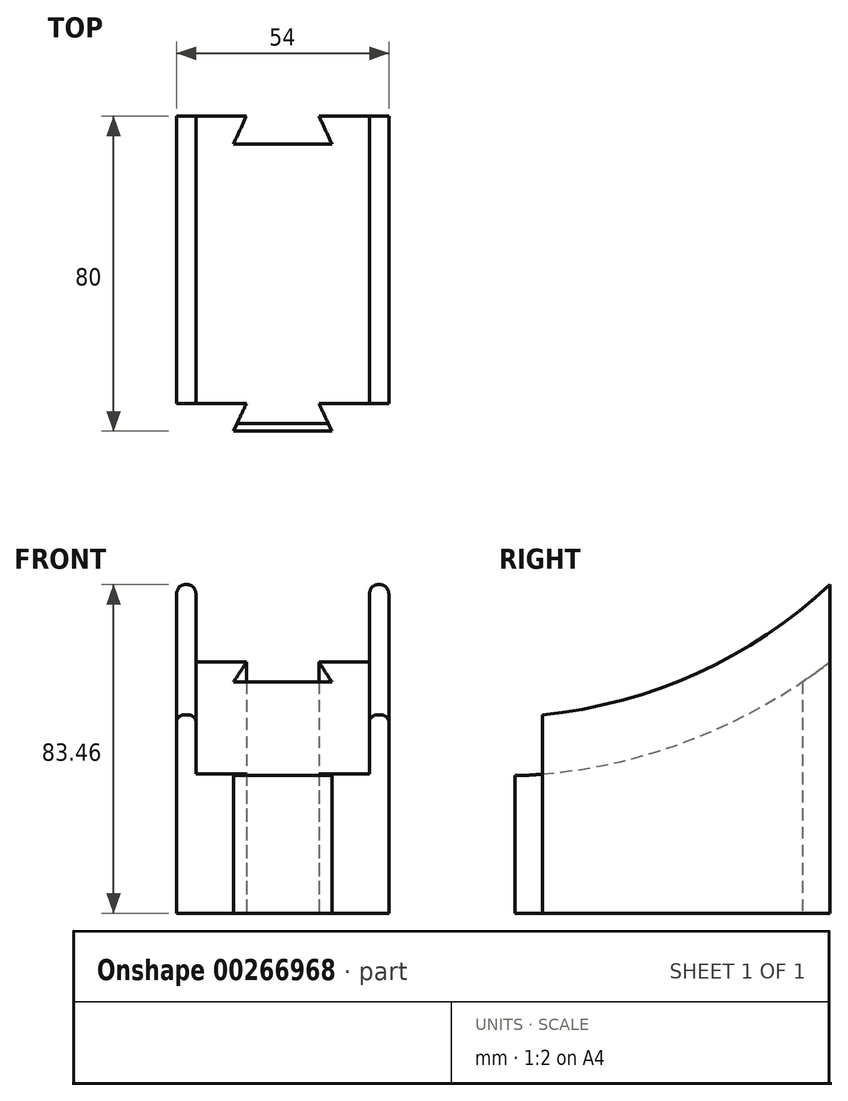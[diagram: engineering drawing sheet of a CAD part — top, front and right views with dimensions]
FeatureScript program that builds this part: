
annotation { "Feature Type Name" : "Feature", "Feature Type Description" : "" }
export const myFeature = defineFeature(function(context is Context, id is Id, definition is map)
    precondition{}
    {
        {
            var Q0;
            Q0=qCreatedBy(makeId("Right.planeOp"),FACE);
            var sketch = newSketch(context, id + "F0", { "sketchPlane" : qUnion([Q0])});
            skLineSegment(sketch, "E0.top", {"start": v(0, 120) * mm, "end": v(-45, 120) * mm});
            skLineSegment(sketch, "E0.left", {"start": v(0, 0) * mm, "end": v(0, 120) * mm});
            skLineSegment(sketch, "E1.top", {"start": v(0, 0) * mm, "end": v(-150, 0) * mm});
            skArc(sketch, "E2", {"start": v(-150, 50) * mm, "mid": v(-88.02, 70.78) * mm, "end": v(-45, 120) * mm});
            skLineSegment(sketch, "E3", {"start": v(-150, 50) * mm, "end": v(-150, 0) * mm});
            skSolve(sketch);
        }
        {
            var Q0;
            Q0=makeQuery(id+"F0.imprint","IMPRINT",FACE,{"disambiguationData":[TD([[makeQuery(id+"F0.imprint","IMPRINT",EDGE,{"derivedFrom":sQuery(id+"F0.wireOp",EDGE,"E0.bottom")}),-1.0]])]});
            var Q1;
            Q1=makeQuery(id+"F0.imprint","IMPRINT",FACE,{"disambiguationData":[TD([[makeQuery(id+"F0.imprint","IMPRINT",EDGE,{"derivedFrom":sQuery(id+"F0.wireOp",EDGE,"E0.top")}),1.0]])]});
            extrude(context, id + "F1", {"entities" : qUnion([Q0, Q1]), "depth" : 27 * mm});
        }
        {
            var Q0;
            Q0=makeQuery(id+"F1.opExtrude","SWEPT_BODY",BODY,{"disambiguationData":[OSD([sQuery(id+"F0.wireOp",EDGE,"E0.bottom"),sQuery(id+"F0.wireOp",EDGE,"E0.top"),sQuery(id+"F0.wireOp",EDGE,"E0.left"),sQuery(id+"F0.wireOp",EDGE,"E1.bottom"),sQuery(id+"F0.wireOp",EDGE,"E1.top"),sQuery(id+"F0.wireOp",EDGE,"E1.right"),sQuery(id+"F0.wireOp",EDGE,"E2")])]});
            var Q1;
            Q1=qCreatedBy(makeId("Right.planeOp"),FACE);
            mirror(context, id + "F2", {"operationType" : NewBodyOperationType.ADD, "entities" : qUnion([Q0]), "mirrorPlane" : qUnion([Q1])});
        }
        {
            var Q0;
            Q0=qCreatedBy(makeId("Right.planeOp"),FACE);
            var sketch = newSketch(context, id + "F3", { "sketchPlane" : qUnion([Q0])});
            skArc(sketch, "E4.0", {"start": v(-150, 34.98) * mm, "mid": v(-83.11, 56.1) * mm, "end": v(-34.86, 107) * mm});
            skLineSegment(sketch, "E5.0", {"start": v(-4.86, 107) * mm, "end": v(-34.86, 107) * mm});
            skLineSegment(sketch, "E6", {"start": v(-4.86, 107) * mm, "end": v(-4.86, 120) * mm});
            skLineSegment(sketch, "E7", {"start": v(-150, 34.98) * mm, "end": v(-150, 58.04) * mm});
            skArc(sketch, "E8.0", {"start": v(-150, 58.04) * mm, "mid": v(-93.92, 76.5) * mm, "end": v(-54, 120) * mm});
            skLineSegment(sketch, "E9", {"start": v(-54, 120) * mm, "end": v(-4.86, 120) * mm});
            skSolve(sketch);
        }
        {
            var Q0;
            Q0=qSketchRegion(id+"F3",true);
            extrude(context, id + "F4", {"entities" : qUnion([Q0]), "operationType" : NewBodyOperationType.REMOVE, "oppositeDirection" : true, "depth" : 22 * mm});
        }
        {
            var Q0;
            Q0=qSketchRegion(id+"F3",true);
            extrude(context, id + "F5", {"entities" : qUnion([Q0]), "operationType" : NewBodyOperationType.REMOVE, "depth" : 22 * mm});
        }
        {
            var Q0;
            Q0=qCreatedBy(makeId("Right.planeOp"),FACE);
            var sketch = newSketch(context, id + "F6", { "sketchPlane" : qUnion([Q0])});
            skLineSegment(sketch, "E10.bottom", {"start": v(-150, 0) * mm, "end": v(-240, 0) * mm});
            skLineSegment(sketch, "E10.top", {"start": v(-150, 50) * mm, "end": v(-240, 50) * mm});
            skLineSegment(sketch, "E10.left", {"start": v(-150, 0) * mm, "end": v(-150, 50) * mm});
            skLineSegment(sketch, "E10.right", {"start": v(-240, 0) * mm, "end": v(-240, 50) * mm});
            skSolve(sketch);
        }
        {
            var Q0;
            Q0=makeQuery(id+"F6.imprint","IMPRINT",FACE,{"disambiguationData":[TD([[makeQuery(id+"F6.imprint","IMPRINT",EDGE,{"derivedFrom":sQuery(id+"F6.wireOp",EDGE,"E10.bottom")}),-1.0]])]});
            extrude(context, id + "F7", {"entities" : qUnion([Q0]), "operationType" : NewBodyOperationType.ADD, "endBound" : BoundingType.SYMMETRIC, "oppositeDirection" : true, "depth" : 150 * mm});
        }
        {
            var Q0;
            Q0=makeQuery(id+"F7.opExtrude","SWEPT_FACE",FACE,{"disambiguationData":[OSD([sQuery(id+"F6.wireOp",EDGE,"E10.top")])]});
            var sketch = newSketch(context, id + "F8", { "sketchPlane" : qUnion([Q0])});
            skLineSegment(sketch, "E11.bottom", {"start": v(-70, -155) * mm, "end": v(70, -155) * mm});
            skLineSegment(sketch, "E11.top", {"start": v(-70, -235) * mm, "end": v(70, -235) * mm});
            skLineSegment(sketch, "E11.left", {"start": v(-70, -155) * mm, "end": v(-70, -235) * mm});
            skLineSegment(sketch, "E11.right", {"start": v(70, -155) * mm, "end": v(70, -235) * mm});
            skPoint(sketch, "E11.middle", {"position": v(0, -195) * mm});
            skSolve(sketch);
        }
        {
            var Q0;
            Q0=makeQuery(id+"F8.imprint","IMPRINT",FACE,{"disambiguationData":[TD([[makeQuery(id+"F8.imprint","IMPRINT",EDGE,{"derivedFrom":sQuery(id+"F8.wireOp",EDGE,"E11.bottom")}),-1.0]])]});
            extrude(context, id + "F9", {"entities" : qUnion([Q0]), "operationType" : NewBodyOperationType.REMOVE, "oppositeDirection" : true, "depth" : 45 * mm});
        }
        {
            var Q0;
            {var subQ5=sQuery(id+"F3.wireOp",EDGE,"E4.0");Q0=makeQuery(id+"F7.boolean.opBoolean","SPLIT",FACE,{"disambiguationData":[TD([makeQuery(id+"F4.boolean.opBoolean","COPY",FACE,{"derivedFrom":makeQuery(id+"F4.opExtrude","SWEPT_FACE",FACE,{"disambiguationData":[OSD([subQ5])]})})])],"derivedFrom":makeQuery(id+"F7.opExtrude","SWEPT_FACE",FACE,{"disambiguationData":[OSD([sQuery(id+"F6.wireOp",EDGE,"E10.left")])]})});}
            extrude(context, id + "F10", {"entities" : qUnion([Q0]), "operationType" : NewBodyOperationType.REMOVE, "oppositeDirection" : true, "depth" : 25 * mm});
        }
        {
            var Q0;
            Q0=makeQuery(id+"F7.opExtrude","CAP_EDGE",EDGE,{"disambiguationData":[OSD([sQuery(id+"F6.wireOp",EDGE,"E10.right")])],"isStart":true});
            var Q1;
            Q1=makeQuery(id+"F7.opExtrude","CAP_EDGE",EDGE,{"disambiguationData":[OSD([sQuery(id+"F6.wireOp",EDGE,"E10.left")])],"isStart":true});
            var Q2;
            Q2=makeQuery(id+"F7.opExtrude","CAP_EDGE",EDGE,{"disambiguationData":[OSD([sQuery(id+"F6.wireOp",EDGE,"E10.right")])],"isStart":false});
            var Q3;
            Q3=makeQuery(id+"F7.opExtrude","CAP_EDGE",EDGE,{"disambiguationData":[OSD([sQuery(id+"F6.wireOp",EDGE,"E10.left")])],"isStart":false});
            var Q4;
            Q4=makeQuery(id+"F1.opExtrude","CAP_EDGE",EDGE,{"disambiguationData":[OSD([sQuery(id+"F0.wireOp",EDGE,"E2")])],"isStart":false});
            var Q5;
            {var subQ2=sQuery(id+"F6.wireOp",EDGE,"E10.left");var subQ3=sQuery(id+"F6.wireOp",EDGE,"E10.top");Q5=makeQuery(id+"F7.boolean.opBoolean","SPLIT",EDGE,{"disambiguationData":[TD([makeQuery(id+"F7.opExtrude","CAP_FACE",FACE,{"disambiguationData":[OSD([sQuery(id+"F6.wireOp",EDGE,"E10.bottom"),subQ3,subQ2,sQuery(id+"F6.wireOp",EDGE,"E10.right")])],"isStart":true})])],"derivedFrom":makeQuery(id+"F7.opExtrude","SWEPT_EDGE",EDGE,{"disambiguationData":[OSD([subQ3,subQ2])]})});}
            var Q6;
            Q6=makeQuery(id+"F7.opExtrude","CAP_EDGE",EDGE,{"disambiguationData":[OSD([sQuery(id+"F6.wireOp",EDGE,"E10.top")])],"isStart":true});
            var Q7;
            Q7=makeQuery(id+"F7.opExtrude","SWEPT_EDGE",EDGE,{"disambiguationData":[OSD([sQuery(id+"F6.wireOp",EDGE,"E10.top"),sQuery(id+"F6.wireOp",EDGE,"E10.right")])]});
            var Q8;
            Q8=makeQuery(id+"F7.opExtrude","CAP_EDGE",EDGE,{"disambiguationData":[OSD([sQuery(id+"F6.wireOp",EDGE,"E10.top")])],"isStart":false});
            var Q9;
            {var subQ2=sQuery(id+"F6.wireOp",EDGE,"E10.left");var subQ3=sQuery(id+"F6.wireOp",EDGE,"E10.top");Q9=makeQuery(id+"F7.boolean.opBoolean","SPLIT",EDGE,{"disambiguationData":[TD([makeQuery(id+"F7.opExtrude","CAP_FACE",FACE,{"disambiguationData":[OSD([sQuery(id+"F6.wireOp",EDGE,"E10.bottom"),subQ3,subQ2,sQuery(id+"F6.wireOp",EDGE,"E10.right")])],"isStart":false})])],"derivedFrom":makeQuery(id+"F7.opExtrude","SWEPT_EDGE",EDGE,{"disambiguationData":[OSD([subQ3,subQ2])]})});}
            var Q10;
            Q10=makeQuery(id+"F2.opPattern","COPY",EDGE,{"derivedFrom":makeQuery(id+"F1.opExtrude","CAP_EDGE",EDGE,{"disambiguationData":[OSD([sQuery(id+"F0.wireOp",EDGE,"E2")])],"isStart":false}),"instanceName":"1"});
            var Q11;
            Q11=makeQuery(id+"F1.opExtrude","CAP_EDGE",EDGE,{"disambiguationData":[OSD([sQuery(id+"F0.wireOp",EDGE,"E0.top")])],"isStart":false});
            var Q12;
            Q12=makeQuery(id+"F2.opPattern","COPY",EDGE,{"derivedFrom":makeQuery(id+"F1.opExtrude","CAP_EDGE",EDGE,{"disambiguationData":[OSD([sQuery(id+"F0.wireOp",EDGE,"E0.top")])],"isStart":false}),"instanceName":"1"});
            var Q13;
            {var subQ0=makeQuery(id+"F1.opExtrude","SWEPT_EDGE",EDGE,{"disambiguationData":[OSD([sQuery(id+"F0.wireOp",EDGE,"E0.top"),sQuery(id+"F0.wireOp",EDGE,"E0.left")])]});Q13=makeQuery(id+"F2.boolean.opBoolean","MERGE",EDGE,{"derivedFrom":[subQ0,makeQuery(id+"F2.opPattern","COPY",EDGE,{"derivedFrom":subQ0,"instanceName":"1"})]});}
            var Q14;
            Q14=makeQuery(id+"F1.opExtrude","CAP_EDGE",EDGE,{"disambiguationData":[OSD([sQuery(id+"F0.wireOp",EDGE,"E0.left")])],"isStart":false});
            var Q15;
            Q15=makeQuery(id+"F2.opPattern","COPY",EDGE,{"derivedFrom":makeQuery(id+"F1.opExtrude","CAP_EDGE",EDGE,{"disambiguationData":[OSD([sQuery(id+"F0.wireOp",EDGE,"E0.left")])],"isStart":false}),"instanceName":"1"});
            fillet(context, id + "F11", {"entities" : qUnion([Q0, Q1, Q2, Q3, Q4, Q5, Q6, Q7, Q8, Q9, Q10, Q11, Q12, Q13, Q14, Q15]), "radius" : 2 * mm, "tangentPropagation" : true, "allowEdgeOverflow" : false});
        }
        {
            var Q0;
            {var subQ0=sQuery(id+"F3.wireOp",EDGE,"E5.0");var subQ1=sQuery(id+"F3.wireOp",EDGE,"E4.0");Q0=makeQuery(id+"F5.boolean.opBoolean","MERGE",EDGE,{"derivedFrom":[makeQuery(id+"F4.boolean.opBoolean","COPY",EDGE,{"derivedFrom":makeQuery(id+"F4.opExtrude","SWEPT_EDGE",EDGE,{"disambiguationData":[OSD([subQ1,subQ0])]})}),makeQuery(id+"F5.opExtrude","SWEPT_EDGE",EDGE,{"disambiguationData":[OSD([subQ1,subQ0])]})]});}
            var Q1;
            Q1=makeQuery(id+"F10.boolean.opBoolean","INTERSECT",EDGE,{"derivedFrom":[makeQuery(id+"F9.boolean.opBoolean","COPY",FACE,{"derivedFrom":makeQuery(id+"F9.opExtrude","SWEPT_FACE",FACE,{"disambiguationData":[OSD([sQuery(id+"F8.wireOp",EDGE,"E11.bottom")])]})}),makeQuery(id+"F10.opExtrude","SWEPT_FACE",FACE,{"disambiguationData":[OSD([sQuery(id+"F3.wireOp",EDGE,"E4.0"),sQuery(id+"F3.wireOp",EDGE,"E7")])]})]});
            fillet(context, id + "F12", {"entities" : qUnion([Q0, Q1]), "radius" : 10 * mm, "tangentPropagation" : true, "allowEdgeOverflow" : false});
        }
        {
            var Q0;
            Q0=makeQuery(id+"F9.boolean.opBoolean","COPY",EDGE,{"derivedFrom":makeQuery(id+"F9.opExtrude","SWEPT_EDGE",EDGE,{"disambiguationData":[OSD([sQuery(id+"F8.wireOp",EDGE,"E11.top"),sQuery(id+"F8.wireOp",EDGE,"E11.left")])]})});
            var Q1;
            Q1=makeQuery(id+"F9.boolean.opBoolean","COPY",EDGE,{"derivedFrom":makeQuery(id+"F9.opExtrude","SWEPT_EDGE",EDGE,{"disambiguationData":[OSD([sQuery(id+"F8.wireOp",EDGE,"E11.bottom"),sQuery(id+"F8.wireOp",EDGE,"E11.left")])]})});
            var Q2;
            Q2=makeQuery(id+"F9.boolean.opBoolean","COPY",EDGE,{"derivedFrom":makeQuery(id+"F9.opExtrude","SWEPT_EDGE",EDGE,{"disambiguationData":[OSD([sQuery(id+"F8.wireOp",EDGE,"E11.top"),sQuery(id+"F8.wireOp",EDGE,"E11.right")])]})});
            var Q3;
            Q3=makeQuery(id+"F9.boolean.opBoolean","COPY",EDGE,{"derivedFrom":makeQuery(id+"F9.opExtrude","SWEPT_EDGE",EDGE,{"disambiguationData":[OSD([sQuery(id+"F8.wireOp",EDGE,"E11.bottom"),sQuery(id+"F8.wireOp",EDGE,"E11.right")])]})});
            var Q4;
            Q4=makeQuery(id+"F9.boolean.opBoolean","COPY",FACE,{"derivedFrom":makeQuery(id+"F9.opExtrude","CAP_FACE",FACE,{"disambiguationData":[OSD([sQuery(id+"F8.wireOp",EDGE,"E11.bottom"),sQuery(id+"F8.wireOp",EDGE,"E11.top"),sQuery(id+"F8.wireOp",EDGE,"E11.left"),sQuery(id+"F8.wireOp",EDGE,"E11.right")])],"isStart":false})});
            var Q5;
            {var subQ0=sQuery(id+"F3.wireOp",EDGE,"E7");Q5=makeQuery(id+"F10.boolean.opBoolean","INTERSECT",EDGE,{"derivedFrom":[makeQuery(id+"F9.boolean.opBoolean","COPY",FACE,{"derivedFrom":makeQuery(id+"F9.opExtrude","SWEPT_FACE",FACE,{"disambiguationData":[OSD([sQuery(id+"F8.wireOp",EDGE,"E11.bottom")])]})}),makeQuery(id+"F10.opExtrude","SWEPT_FACE",FACE,{"disambiguationData":[OSD([subQ0]),TDD([makeQuery(id+"F4.boolean.opBoolean","COPY",EDGE,{"derivedFrom":makeQuery(id+"F4.opExtrude","CAP_EDGE",EDGE,{"disambiguationData":[OSD([subQ0])],"isStart":false})})])]})]});}
            var Q6;
            {var subQ0=sQuery(id+"F3.wireOp",EDGE,"E7");Q6=makeQuery(id+"F10.boolean.opBoolean","INTERSECT",EDGE,{"derivedFrom":[makeQuery(id+"F9.boolean.opBoolean","COPY",FACE,{"derivedFrom":makeQuery(id+"F9.opExtrude","SWEPT_FACE",FACE,{"disambiguationData":[OSD([sQuery(id+"F8.wireOp",EDGE,"E11.bottom")])]})}),makeQuery(id+"F10.opExtrude","SWEPT_FACE",FACE,{"disambiguationData":[OSD([subQ0]),TDD([makeQuery(id+"F5.boolean.opBoolean","COPY",EDGE,{"derivedFrom":makeQuery(id+"F5.opExtrude","CAP_EDGE",EDGE,{"disambiguationData":[OSD([subQ0])],"isStart":false})})])]})]});}
            var Q7;
            {var subQ0=sQuery(id+"F8.wireOp",EDGE,"E11.bottom");Q7=makeQuery(id+"F10.boolean.opBoolean","SPLIT",EDGE,{"disambiguationData":[TD([makeQuery(id+"F9.boolean.opBoolean","COPY",FACE,{"derivedFrom":makeQuery(id+"F9.opExtrude","SWEPT_FACE",FACE,{"disambiguationData":[OSD([sQuery(id+"F8.wireOp",EDGE,"E11.left")])]})})])],"derivedFrom":makeQuery(id+"F9.boolean.opBoolean","COPY",EDGE,{"derivedFrom":makeQuery(id+"F9.opExtrude","CAP_EDGE",EDGE,{"disambiguationData":[OSD([subQ0])],"isStart":true})})});}
            var Q8;
            {var subQ1=sQuery(id+"F8.wireOp",EDGE,"E11.bottom");Q8=makeQuery(id+"F10.boolean.opBoolean","SPLIT",EDGE,{"disambiguationData":[TD([makeQuery(id+"F9.boolean.opBoolean","COPY",FACE,{"derivedFrom":makeQuery(id+"F9.opExtrude","SWEPT_FACE",FACE,{"disambiguationData":[OSD([sQuery(id+"F8.wireOp",EDGE,"E11.right")])]})})])],"derivedFrom":makeQuery(id+"F9.boolean.opBoolean","COPY",EDGE,{"derivedFrom":makeQuery(id+"F9.opExtrude","CAP_EDGE",EDGE,{"disambiguationData":[OSD([subQ1])],"isStart":true})})});}
            var Q9;
            {var subQ0=makeQuery(id+"F1.opExtrude","SWEPT_FACE",FACE,{"disambiguationData":[OSD([sQuery(id+"F0.wireOp",EDGE,"E2")])]});Q9=makeQuery(id+"F4.boolean.opBoolean","INTERSECT",EDGE,{"derivedFrom":[makeQuery(id+"F2.boolean.opBoolean","MERGE",FACE,{"derivedFrom":[subQ0,makeQuery(id+"F2.opPattern","COPY",FACE,{"derivedFrom":subQ0,"instanceName":"1"})]}),makeQuery(id+"F4.opExtrude","CAP_FACE",FACE,{"disambiguationData":[OSD([sQuery(id+"F3.wireOp",EDGE,"E4.0"),sQuery(id+"F3.wireOp",EDGE,"E5.0"),sQuery(id+"F3.wireOp",EDGE,"E6"),sQuery(id+"F3.wireOp",EDGE,"E7"),sQuery(id+"F3.wireOp",EDGE,"E8.0"),sQuery(id+"F3.wireOp",EDGE,"E9")])],"isStart":false})]});}
            var Q10;
            {var subQ0=sQuery(id+"F3.wireOp",EDGE,"E9");var subQ1=sQuery(id+"F3.wireOp",EDGE,"E8.0");var subQ2=sQuery(id+"F3.wireOp",EDGE,"E7");var subQ3=sQuery(id+"F3.wireOp",EDGE,"E6");var subQ4=sQuery(id+"F3.wireOp",EDGE,"E5.0");var subQ5=sQuery(id+"F3.wireOp",EDGE,"E4.0");var subQ6=sQuery(id+"F0.wireOp",EDGE,"E0.top");var subQ8=sQuery(id+"F0.wireOp",EDGE,"E3");var subQ10=sQuery(id+"F0.wireOp",EDGE,"E2");var subQ11=makeQuery(id+"F1.opExtrude","SWEPT_FACE",FACE,{"disambiguationData":[OSD([subQ10])]});Q10=makeQuery(id+"F5.boolean.opBoolean","INTERSECT",EDGE,{"derivedFrom":[makeQuery(id+"F4.boolean.opBoolean","SPLIT",FACE,{"disambiguationData":[TD([makeQuery(id+"F1.opExtrude","CAP_FACE",FACE,{"disambiguationData":[OSD([subQ6,sQuery(id+"F0.wireOp",EDGE,"E0.left"),sQuery(id+"F0.wireOp",EDGE,"E1.top"),subQ10,subQ8])],"isStart":false})])],"derivedFrom":makeQuery(id+"F2.boolean.opBoolean","MERGE",FACE,{"derivedFrom":[subQ11,makeQuery(id+"F2.opPattern","COPY",FACE,{"derivedFrom":subQ11,"instanceName":"1"})]})}),makeQuery(id+"F5.opExtrude","CAP_FACE",FACE,{"disambiguationData":[OSD([subQ5,subQ4,subQ3,subQ2,subQ1,subQ0])],"isStart":false})]});}
            var Q11;
            Q11=makeQuery(id+"F4.boolean.opBoolean","COPY",EDGE,{"derivedFrom":makeQuery(id+"F4.opExtrude","CAP_EDGE",EDGE,{"disambiguationData":[OSD([sQuery(id+"F3.wireOp",EDGE,"E9")])],"isStart":false})});
            var Q12;
            Q12=makeQuery(id+"F5.boolean.opBoolean","COPY",EDGE,{"derivedFrom":makeQuery(id+"F5.opExtrude","CAP_EDGE",EDGE,{"disambiguationData":[OSD([sQuery(id+"F3.wireOp",EDGE,"E9")])],"isStart":false})});
            var Q13;
            {var subQ0=sQuery(id+"F3.wireOp",EDGE,"E9");var subQ1=sQuery(id+"F3.wireOp",EDGE,"E6");Q13=makeQuery(id+"F5.boolean.opBoolean","MERGE",EDGE,{"derivedFrom":[makeQuery(id+"F4.boolean.opBoolean","COPY",EDGE,{"derivedFrom":makeQuery(id+"F4.opExtrude","SWEPT_EDGE",EDGE,{"disambiguationData":[OSD([subQ1,subQ0])]})}),makeQuery(id+"F5.opExtrude","SWEPT_EDGE",EDGE,{"disambiguationData":[OSD([subQ1,subQ0])]})]});}
            fillet(context, id + "F13", {"entities" : qUnion([Q0, Q1, Q2, Q3, Q4, Q5, Q6, Q7, Q8, Q9, Q10, Q11, Q12, Q13]), "radius" : 2 * mm, "tangentPropagation" : true, "allowEdgeOverflow" : false});
        }
        {
            var Q0;
            Q0=qCreatedBy(makeId("Top.planeOp"),FACE);
            var sketch = newSketch(context, id + "F14", { "sketchPlane" : qUnion([Q0])});
            skLineSegment(sketch, "E12", {"start": v(-87.83, -145) * mm, "end": v(-9.24, -145) * mm});
            skLineSegment(sketch, "E13", {"start": v(0, -162.57) * mm, "end": v(0, 0) * mm, "construction": true});
            skLineSegment(sketch, "E14", {"start": v(-9.24, -145) * mm, "end": v(-12.5, -152) * mm});
            skLineSegment(sketch, "E15", {"start": v(-12.5, -152) * mm, "end": v(0, -152) * mm});
            skLineSegment(sketch, "E16", {"start": v(0, -152) * mm, "end": v(0, -145) * mm});
            skLineSegment(sketch, "E17.MirrorCS", {"start": v(9.24, -145) * mm, "end": v(12.5, -152) * mm});
            skLineSegment(sketch, "E18.MirrorCS", {"start": v(12.5, -152) * mm, "end": v(0, -152) * mm});
            skLineSegment(sketch, "E19.trimOffspring", {"start": v(9.24, -145) * mm, "end": v(99.3, -145) * mm});
            skLineSegment(sketch, "E20", {"start": v(-87.83, -145) * mm, "end": v(-87.83, -254.71) * mm});
            skLineSegment(sketch, "E21", {"start": v(-87.83, -254.71) * mm, "end": v(101.8, -254.71) * mm});
            skLineSegment(sketch, "E22", {"start": v(101.8, -254.71) * mm, "end": v(99.3, -145) * mm});
            skSolve(sketch);
        }
        {
            var Q0;
            Q0 = qSketchRegion(id + "F14", true);
            extrude(context, id + "F15", {"entities" : qUnion([Q0]), "operationType" : NewBodyOperationType.REMOVE, "depth" : 60 * mm});
        }
        {
            var Q0;
            Q0=qCreatedBy(makeId("Top.planeOp"),FACE);
            var sketch = newSketch(context, id + "F16", { "sketchPlane" : qUnion([Q0])});
            skLineSegment(sketch, "E23", {"start": v(-59.73, -72) * mm, "end": v(-9.24, -72) * mm});
            skLineSegment(sketch, "E24", {"start": v(0, 0) * mm, "end": v(0, -89.57) * mm, "construction": true});
            skLineSegment(sketch, "E25", {"start": v(-9.24, -72) * mm, "end": v(-12.5, -79) * mm});
            skLineSegment(sketch, "E26", {"start": v(-12.5, -79) * mm, "end": v(0, -79) * mm});
            skLineSegment(sketch, "E27.MirrorCS", {"start": v(9.24, -72) * mm, "end": v(12.5, -79) * mm});
            skLineSegment(sketch, "E28.MirrorCS", {"start": v(12.5, -79) * mm, "end": v(0, -79) * mm});
            skLineSegment(sketch, "E29.trimOffspring", {"start": v(9.24, -72) * mm, "end": v(47.95, -72) * mm});
            skLineSegment(sketch, "E30", {"start": v(-59.73, -72) * mm, "end": v(-59.73, 11.94) * mm});
            skLineSegment(sketch, "E31", {"start": v(-59.73, 11.94) * mm, "end": v(46.74, 11.94) * mm});
            skLineSegment(sketch, "E32", {"start": v(46.74, 11.94) * mm, "end": v(47.95, -72) * mm});
            skSolve(sketch);
        }
        {
            var Q0;
            Q0 = qSketchRegion(id + "F16", true);
            extrude(context, id + "F17", {"entities" : qUnion([Q0]), "operationType" : NewBodyOperationType.REMOVE, "depth" : 150 * mm});
        }
    });
